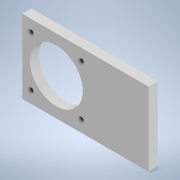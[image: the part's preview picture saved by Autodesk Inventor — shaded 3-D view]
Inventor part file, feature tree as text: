
AUTODESK INVENTOR PART (.ipt)
format: ipt  version: 2020 (Build 240168000, 168)  size: 130,048 bytes
history: native  units: in
note: dims shown in document units (in); Inventor stores cm internally (conversion verified against a paired STEP export)
features: other x4, extrude x2, sketch x2, reference x2, projected_geometry x1
ambient origin geometry x8: Origin, YZ Plane, XZ Plane, XY Plane, X Axis, Y Axis, Z Axis, Center Point
bodies: Solid1 (feature_tree)
feature tree (11):
  extrude  "Extrusion1"  Depth=0.5in TaperAngle=0.0deg
  extrude  "Extrusion2"  Depth=0.375in TaperAngle=0.0deg
  sketch  "Sketch1"  dims[d0=4.0in d1=0.5in d2=0.0in]
  reference  "Reference1"
  reference  "Reference2"
  sketch  "Sketch2"  dims[d3=0.75in d4=0.375in d5=0.0in]
  projected_geometry  "Projected Loop1"
  other  "<userpath>\Desktop\PnP Machine\PnP Machine.iam"
  other  "PnP Machine.iam"
  other  "ST8918L4508-A:1"
  other  "Corner Stand Extension:1"
